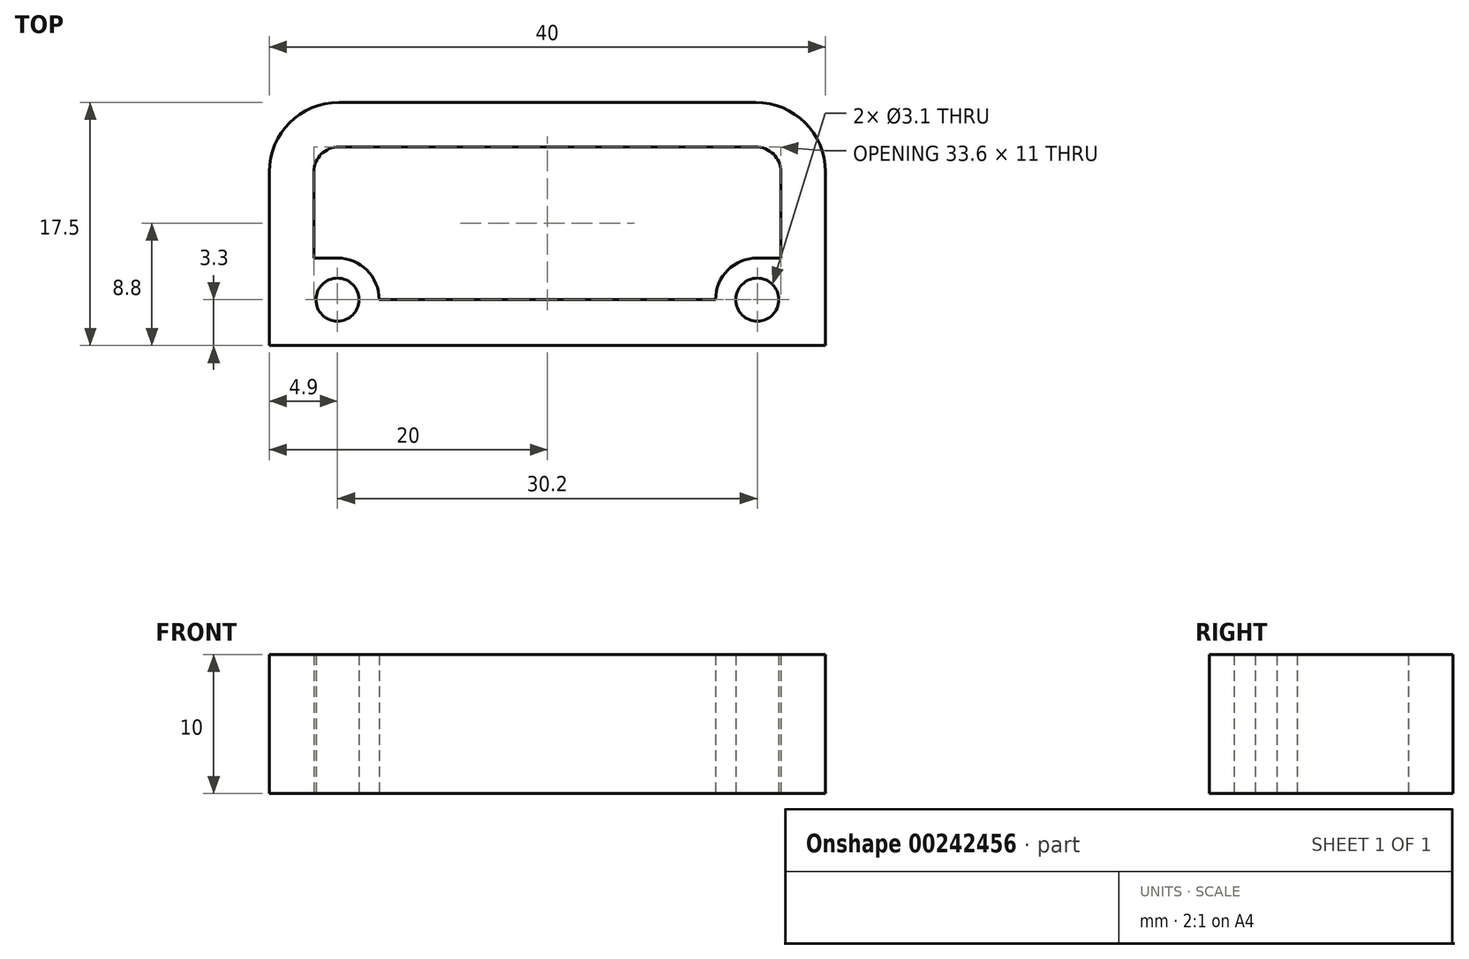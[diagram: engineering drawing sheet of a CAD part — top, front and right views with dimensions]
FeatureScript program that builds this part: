
annotation { "Feature Type Name" : "Feature", "Feature Type Description" : "" }
export const myFeature = defineFeature(function(context is Context, id is Id, definition is map)
    precondition{}
    {
        {
            var Q0;
            Q0=qCreatedBy(makeId("Top.planeOp"),FACE);
            var sketch = newSketch(context, id + "F0", { "sketchPlane" : qUnion([Q0])});
            skLineSegment(sketch, "E0.bottom", {"start": v(20, -8.75) * mm, "end": v(-20, -8.75) * mm});
            skLineSegment(sketch, "E0.top", {"start": v(15, 8.75) * mm, "end": v(-15, 8.75) * mm});
            skLineSegment(sketch, "E0.left", {"start": v(20, -8.75) * mm, "end": v(20, 3.75) * mm});
            skLineSegment(sketch, "E0.right", {"start": v(-20, -8.75) * mm, "end": v(-20, 3.75) * mm});
            skPoint(sketch, "E0.middle", {"position": v(0, 0) * mm});
            skLineSegment(sketch, "E1", {"start": v(-20, -5.45) * mm, "end": v(20, -5.45) * mm, "construction": true});
            skCircle(sketch, "E2", {"center": v(-15.1, -5.45) * mm, "radius": 1.55 * mm});
            skCircle(sketch, "E3", {"center": v(15.1, -5.45) * mm, "radius": 1.55 * mm});
            skLineSegment(sketch, "E4", {"start": v(0, 8.75) * mm, "end": v(0, -8.75) * mm, "construction": true});
            skPoint(sketch, "E5.visualSharp", {"position": v(-20, 8.75) * mm});
            skArc(sketch, "E5.filletArc", {"start": v(-15, 8.75) * mm, "mid": v(-18.54, 7.29) * mm, "end": v(-20, 3.75) * mm});
            skPoint(sketch, "E6.visualSharp", {"position": v(20, 8.75) * mm});
            skArc(sketch, "E6.filletArc", {"start": v(20, 3.75) * mm, "mid": v(18.54, 7.29) * mm, "end": v(15, 8.75) * mm});
            skLineSegment(sketch, "E7.0", {"start": v(16.8, -8.75) * mm, "end": v(16.8, 3.75) * mm});
            skLineSegment(sketch, "E7.1", {"start": v(-16.8, -8.75) * mm, "end": v(-16.8, 3.75) * mm});
            skArc(sketch, "E7.2", {"start": v(-15, 5.55) * mm, "mid": v(-16.27, 5.02) * mm, "end": v(-16.8, 3.75) * mm});
            skLineSegment(sketch, "E7.3", {"start": v(15, 5.55) * mm, "end": v(-15, 5.55) * mm});
            skArc(sketch, "E7.4", {"start": v(16.8, 3.75) * mm, "mid": v(16.27, 5.02) * mm, "end": v(15, 5.55) * mm});
            skLineSegment(sketch, "E8", {"start": v(-13.55, -5.45) * mm, "end": v(13.55, -5.45) * mm});
            skArc(sketch, "E9", {"start": v(-12.1, -5.45) * mm, "mid": v(-13.7, -2.8) * mm, "end": v(-16.8, -2.98) * mm});
            skArc(sketch, "E10.MirrorCS", {"start": v(12.1, -5.45) * mm, "mid": v(13.7, -2.8) * mm, "end": v(16.8, -2.98) * mm});
            skLineSegment(sketch, "E11", {"start": v(-15.1, -2.45) * mm, "end": v(-16.8, -2.45) * mm});
            skLineSegment(sketch, "E12.MirrorCS", {"start": v(15.1, -2.45) * mm, "end": v(16.8, -2.45) * mm});
            skSolve(sketch);
        }
        {
            var Q0;
            Q0=makeQuery(id+"F0.imprint","IMPRINT",FACE,{"disambiguationData":[TD([[makeQuery(id+"F0.imprint","IMPRINT",EDGE,{"derivedFrom":sQuery(id+"F0.wireOp",EDGE,"E0.top")}),1.0]])]});
            var Q1;
            Q1=makeQuery(id+"F0.imprint","IMPRINT",FACE,{"disambiguationData":[TD([[makeQuery(id+"F0.imprint","IMPRINT",EDGE,{"derivedFrom":sQuery(id+"F0.wireOp",EDGE,"E2")}),-1.0]])]});
            var Q2;
            {var subQ3=sQuery(id+"F0.wireOp",EDGE,"E11");Q2=makeQuery(id+"F0.imprint","IMPRINT",FACE,{"disambiguationData":[TD([[makeQuery(id+"F0.imprint","IMPRINT",EDGE,{"derivedFrom":subQ3}),1.0]])]});}
            var Q3;
            {var subQ3=sQuery(id+"F0.wireOp",EDGE,"E12.MirrorCS");Q3=makeQuery(id+"F0.imprint","IMPRINT",FACE,{"disambiguationData":[TD([[makeQuery(id+"F0.imprint","IMPRINT",EDGE,{"derivedFrom":subQ3}),-1.0]])]});}
            extrude(context, id + "F1", {"entities" : qUnion([Q0, Q1, Q2, Q3]), "depth" : 10 * mm, "offsetDistance" : 25 * mm});
        }
    });
